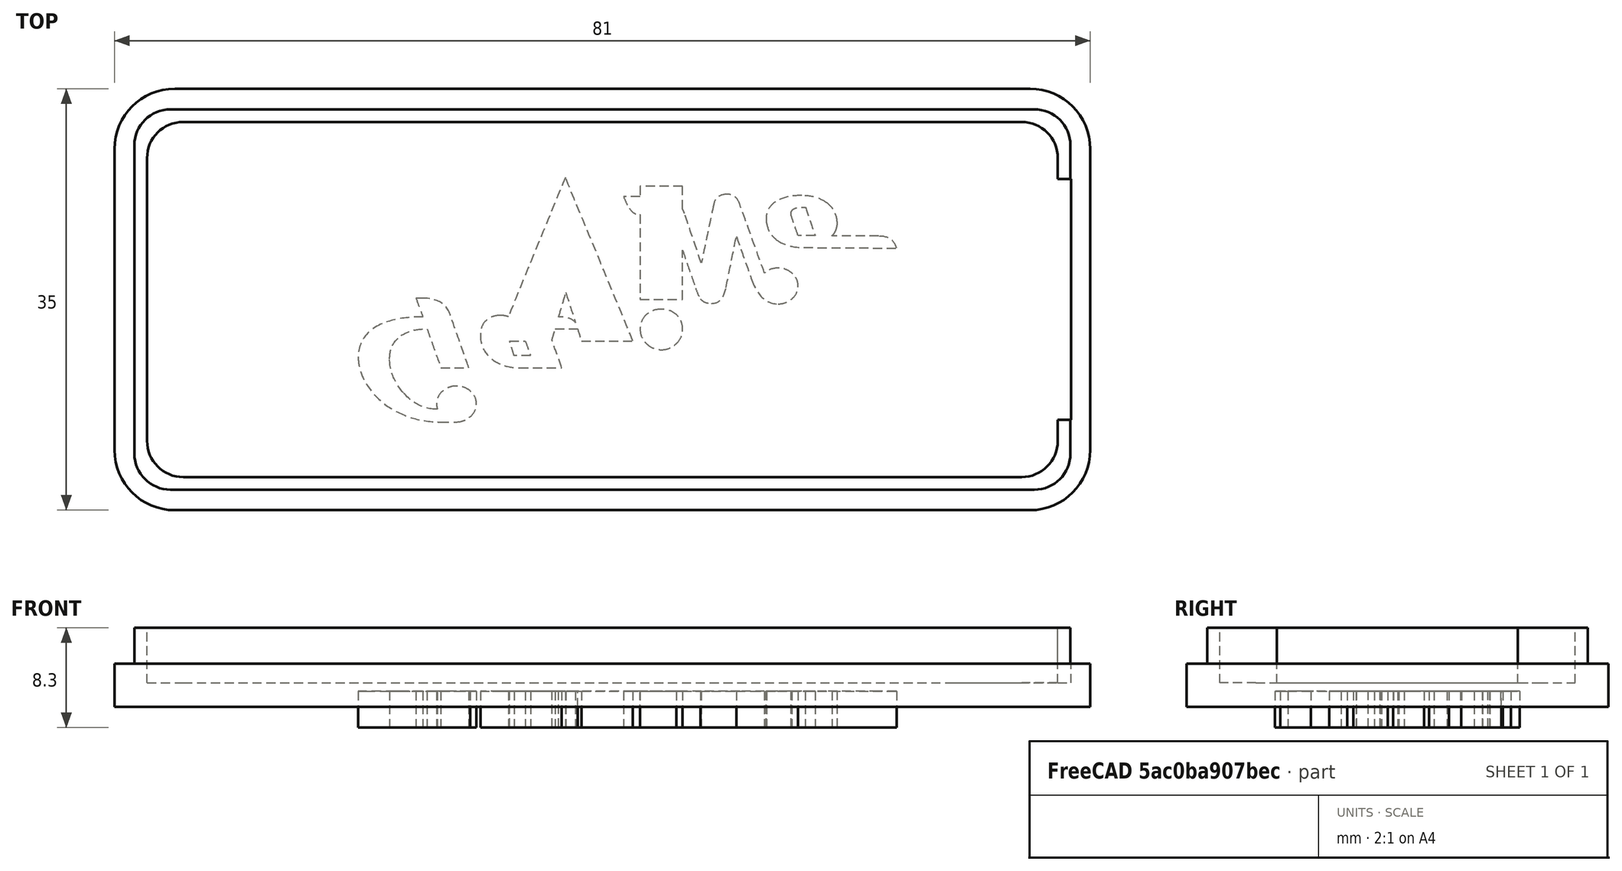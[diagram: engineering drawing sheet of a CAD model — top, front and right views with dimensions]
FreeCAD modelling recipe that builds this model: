
FCSTD DOCUMENT  (FreeCAD 0.16R6712 (Git))
Label: TapaCajaRasp
License: CreativeCommons Attribution-ShareAlike
LicenseURL: http://creativecommons.org/licenses/by-sa/4.0/
objects: Part::Box×5, Part::Cut×3, Part::Fillet×3, Part::Feature×2, Part::MultiFuse×1
note: 14 computed .brp shape members not serialized (recipe doc carries the construction recipe); baked Part::Feature solids carry a one-line shape summary decoded from their .brp

FEATURE [Part::Box] Box  label="Cubo"
  Height = 3.6
  Length = 81
  Placement = pos=(-40.5,-17.5,0) rot=(0,0,1;0rad)
  Width = 35
FEATURE [Part::Box] Box001  label="Cubo001"
  Height = 4.6
  Length = 77.7
  Placement = pos=(-38.85,-15.8,2) rot=(0,0,1;0rad)
  Width = 31.6
FEATURE [Part::Box] Box002  label="Cubo002"
  Height = 7.2
  Length = 75.6
  Placement = pos=(-37.8,-14.75,2) rot=(0,0,1;0rad)
  Width = 29.5
FEATURE [Part::MultiFuse] Fusion
  Shapes = -> [Box,Box001]
FEATURE [Part::Cut] Cut
  Base = -> Fusion
  Tool = -> Box002
FEATURE [Part::Fillet] Fillet
  Base = -> Cut
  Edges = 4 edges r=5: [Edge1,Edge3,Edge6,Edge15]
FEATURE [Part::Fillet] Fillet001
  Base = -> Fillet
  Edges = 4 edges r=3: [Edge41,Edge42,Edge44,Edge46]
FEATURE [Part::Fillet] Fillet002
  Base = -> Fillet001
  Edges = 4 edges r=3: [Edge29,Edge30,Edge32,Edge34]
FEATURE [Part::Feature] Clone001  label="Clone of Fusion001"
  Placement = pos=(-21,-11,1) rot=(1,0,0;3.14159rad)
  shape: bbox 44.68 x 20.32 x 3 mm, 129 faces, 5 solids (baked)
FEATURE [Part::Box] Box003  label="Cubo003"
  Height = 10
  Length = 10
  Placement = pos=(30.5,-10,3.6) rot=(0,0,1;0rad)
  Width = 20
FEATURE [Part::Cut] Cut001
  Base = -> Fillet002
  Tool = -> Box003
FEATURE [Part::Box] Box004  label="Cubo004"
  Height = 10
  Length = 10
  Placement = pos=(28.9,-10,2) rot=(0,0,1;0rad)
  Width = 20
FEATURE [Part::Cut] Cut002  label="Tapa"
  Base = -> Cut001
  Tool = -> Box004
FEATURE [Part::Feature] Cut002001  label="csTapa"
  shape: bbox 81 x 35 x 6.6 mm, 38 faces (baked)
